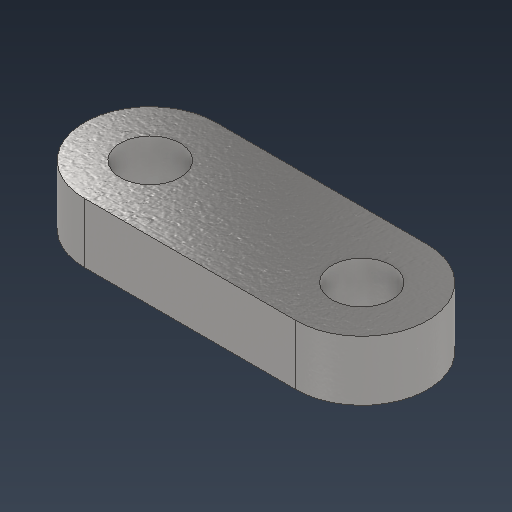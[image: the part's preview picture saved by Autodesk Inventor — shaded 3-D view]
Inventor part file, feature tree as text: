
AUTODESK INVENTOR PART (.ipt)
format: ipt  version: 2021 (Build 250183000, 183)  size: 174,592 bytes
history: native  units: mm
features: sketch x2, extrude x1, hole x1
ambient origin geometry x8: Origin, YZ Plane, XZ Plane, XY Plane, X Axis, Y Axis, Z Axis, Center Point
bodies: Solid1 (feature_tree)
feature tree (4):
  extrude  "Extrusion1"  Depth=5.5mm
  hole  "Hole1"  [1 undecoded]
  sketch  "Sketch1"  dims[d0=11.0mm d1=5.5mm]
  sketch  "Sketch2"  dims[d2=17.686mm d3=5.0mm d4=0.0mm d5=0.0mm d6=0.0mm d7=0.0mm d8=0.0mm d9=5.0mm d10=6.0mm d11=4.0mm d12=2.0mm d13=90.0deg d14=8.0mm d15=20.594885mm]
note: 1 required parameter value undecoded (feature->parameter linkage not recoverable at this tier; creation-order binding heuristic only, values carry confidence <= 0.55)
